# Revit family: РВК_Тройник комбинированный НР
name_source: partatom
category: Соединительные детали трубопроводов
revit_build: Autodesk Revit 2016 (Build: 20150714_1515(x64)
units: mm (PartAtom-declared; Revit-internal decimal feet)

## family parameters
Всегда вертикально = Да
На основе рабочей плоскости = Нет
Общий = Нет
При загрузке вырезать с полостями = Нет
Размер круглого соединителя = Использовать радиус
Тип детали = Тройник

## types (5) — shared parameters
ADSK_Завод-изготовитель = РВК
F = 20 мм
H = 12 мм
Q = 11 мм
Материал стальной части = РВК_Сталь хромированная
Материал фитинга = РВК_Полипропилен PPR

## per-type parameters (varying)
| type | A | B | D | DN | E | G | GN | L1 | L2 | R | g |
| Тройник комбинированный D32-1/2''-32 НР | 18 мм | 41 мм | 32 мм | 32 мм | 41 мм | 16 мм | 20 мм | 70 мм | 35 мм | 16 мм | 10 мм |
| Тройник комбинированный D25-3/4''-25 НР | 17 мм | 42 мм | 25 мм | 25 мм | 41 мм | 20 мм | 25 мм | 62 мм | 33 мм | 13 мм | 13 мм |
| Тройник комбинированный D25-1/2''-25 НР | 17 мм | 34 мм | 25 мм | 25 мм | 35 мм | 16 мм | 20 мм | 59 мм | 30 мм | 13 мм | 10 мм |
| Тройник комбинированный D20-3/4''-20 НР | 15 мм | 29 мм | 20 мм | 20 мм | 40 мм | 20 мм | 25 мм | 59 мм | 30 мм | 10 мм | 13 мм |
| Тройник комбинированный D20-1/2''-20 НР | 15 мм | 29 мм | 20 мм | 20 мм | 35 мм | 16 мм | 20 мм | 52 мм | 28 мм | 10 мм | 10 мм |
